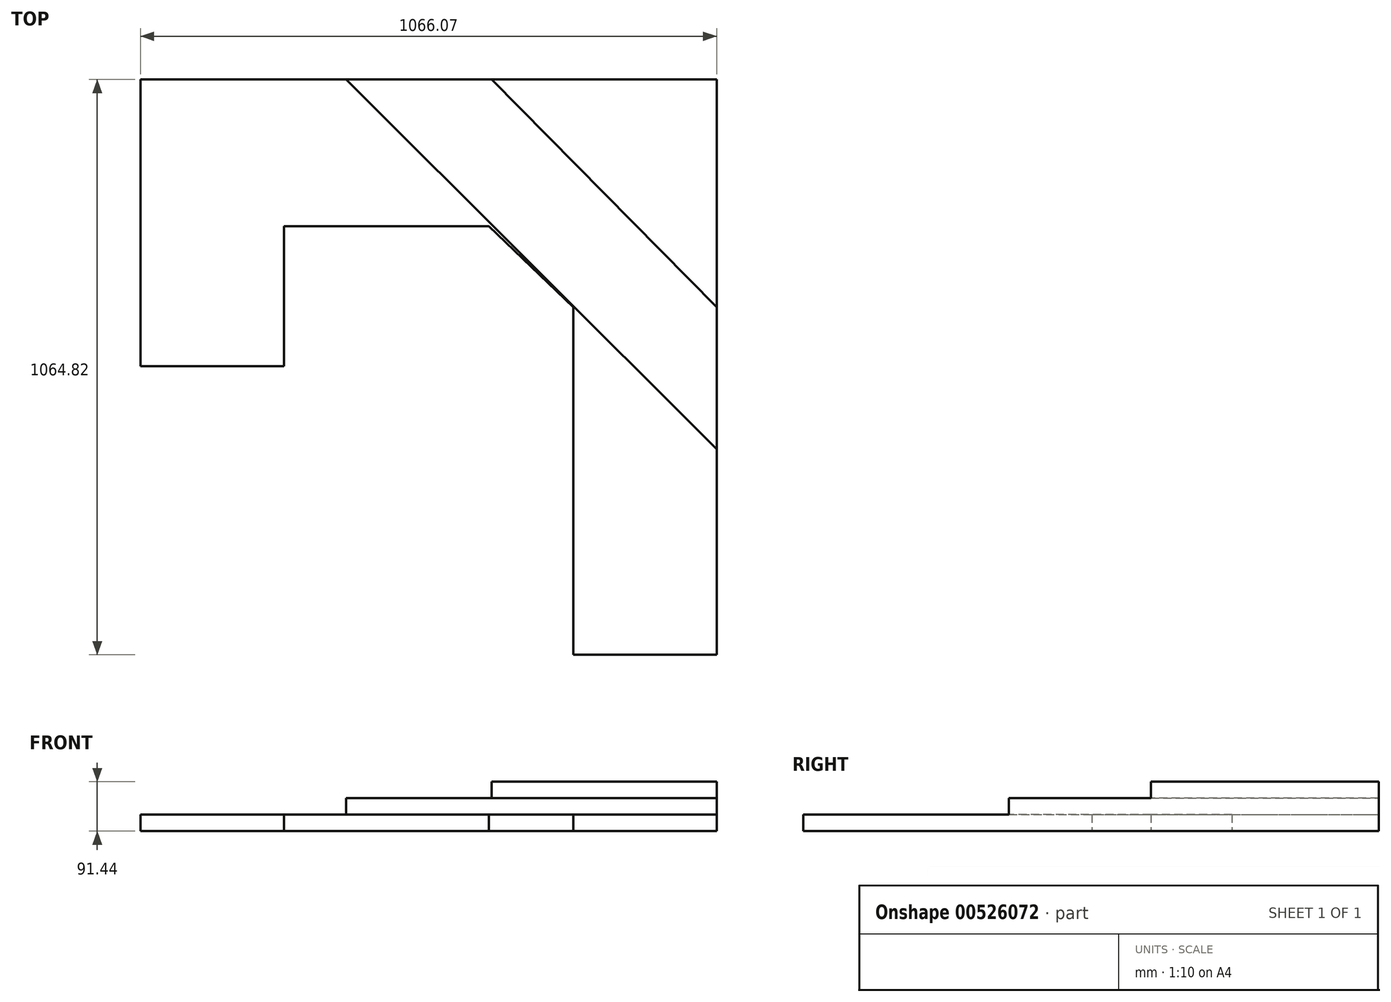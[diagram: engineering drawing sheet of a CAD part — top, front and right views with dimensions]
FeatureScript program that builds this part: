
annotation { "Feature Type Name" : "Feature", "Feature Type Description" : "" }
export const myFeature = defineFeature(function(context is Context, id is Id, definition is map)
    precondition{}
    {
        {
            var Q0;
            Q0=qCreatedBy(makeId("Top.planeOp"),FACE);
            var sketch = newSketch(context, id + "F0", { "sketchPlane" : qUnion([Q0])});
            skLineSegment(sketch, "E0", {"start": v(-1066.07, -530.35) * mm, "end": v(-1066.07, 0) * mm});
            skLineSegment(sketch, "E1", {"start": v(-1066.07, 0) * mm, "end": v(-1066.07, -530.35) * mm});
            skLineSegment(sketch, "E2", {"start": v(-1066.07, -530.35) * mm, "end": v(-800.71, -530.35) * mm});
            skLineSegment(sketch, "E3", {"start": v(-800.71, -530.35) * mm, "end": v(-800.71, -271.25) * mm});
            skLineSegment(sketch, "E4", {"start": v(-800.71, -271.25) * mm, "end": v(-421.45, -271.25) * mm});
            skLineSegment(sketch, "E5", {"start": v(-421.45, -271.25) * mm, "end": v(-264.99, -421.45) * mm});
            skLineSegment(sketch, "E6", {"start": v(-264.99, -421.45) * mm, "end": v(-264.99, -1064.82) * mm});
            skLineSegment(sketch, "E7", {"start": v(-264.99, -1064.82) * mm, "end": v(0, -1064.82) * mm});
            skLineSegment(sketch, "E8", {"start": v(0, -1064.82) * mm, "end": v(0, 0) * mm});
            skLineSegment(sketch, "E9", {"start": v(0, 0) * mm, "end": v(-1066.07, 0) * mm});
            skSolve(sketch);
        }
        {
            var Q0;
            Q0=qSketchRegion(id+"F0",true);
            extrude(context, id + "F1", {"entities" : qUnion([Q0]), "depth" : 30.48 * mm});
        }
        {
            var Q0;
            Q0=qCreatedBy(makeId("Top.planeOp"),FACE);
            var sketch = newSketch(context, id + "F2", { "sketchPlane" : qUnion([Q0])});
            skLineSegment(sketch, "E10", {"start": v(-685.56, 0) * mm, "end": v(0, -684.3) * mm});
            skLineSegment(sketch, "E11", {"start": v(0, -684.3) * mm, "end": v(0, 0) * mm});
            skLineSegment(sketch, "E12", {"start": v(0, 0) * mm, "end": v(-685.56, 0) * mm});
            skSolve(sketch);
        }
        {
            var Q0;
            Q0=qSketchRegion(id+"F2",true);
            extrude(context, id + "F3", {"entities" : qUnion([Q0]), "operationType" : NewBodyOperationType.ADD, "depth" : 60.96 * mm});
        }
        {
            var Q0;
            Q0=qCreatedBy(makeId("Top.planeOp"),FACE);
            var sketch = newSketch(context, id + "F4", { "sketchPlane" : qUnion([Q0])});
            skLineSegment(sketch, "E13", {"start": v(-416.44, 0) * mm, "end": v(0, -421.45) * mm});
            skLineSegment(sketch, "E14", {"start": v(0, -421.45) * mm, "end": v(0, 0) * mm});
            skLineSegment(sketch, "E15", {"start": v(0, 0) * mm, "end": v(-416.44, 0) * mm});
            skSolve(sketch);
        }
        {
            var Q0;
            Q0=qSketchRegion(id+"F4",true);
            extrude(context, id + "F5", {"entities" : qUnion([Q0]), "operationType" : NewBodyOperationType.ADD, "depth" : 91.44 * mm});
        }
    });
